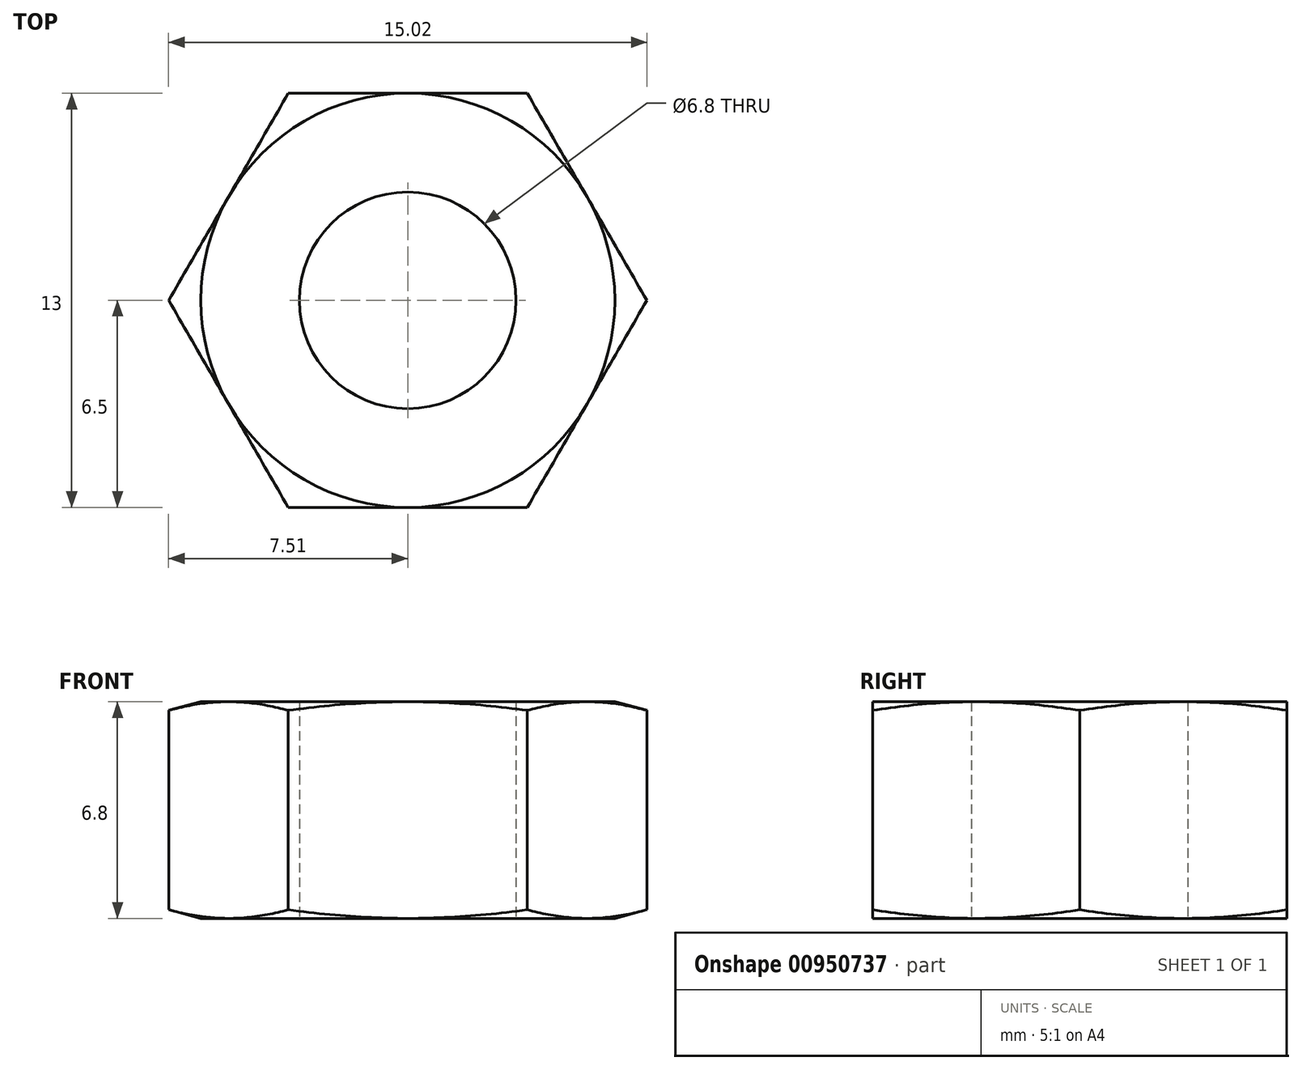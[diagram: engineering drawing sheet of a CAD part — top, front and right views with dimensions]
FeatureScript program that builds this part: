
annotation { "Feature Type Name" : "Feature", "Feature Type Description" : "" }
export const myFeature = defineFeature(function(context is Context, id is Id, definition is map)
    precondition{}
    {
        {
            var Q0;
            Q0=qCreatedBy(makeId("Top.planeOp"),FACE);
            var sketch = newSketch(context, id + "F0", { "sketchPlane" : qUnion([Q0])});
            skCircle(sketch, "E0.cCircle", {"center": v(0, 0) * mm, "radius": 6.5 * mm, "construction": true});
            skLineSegment(sketch, "E0.0", {"start": v(3.75, -6.5) * mm, "end": v(-3.75, -6.5) * mm});
            skLineSegment(sketch, "E0.1", {"start": v(-3.75, -6.5) * mm, "end": v(-7.5, 0) * mm});
            skLineSegment(sketch, "E0.2", {"start": v(-7.5, 0) * mm, "end": v(-3.75, 6.5) * mm});
            skLineSegment(sketch, "E0.3", {"start": v(-3.75, 6.5) * mm, "end": v(3.75, 6.5) * mm});
            skLineSegment(sketch, "E0.4", {"start": v(3.75, 6.5) * mm, "end": v(7.5, 0) * mm});
            skLineSegment(sketch, "E0.5", {"start": v(7.5, 0) * mm, "end": v(3.75, -6.5) * mm});
            skPoint(sketch, "E0.0.midPoint", {"position": v(0, -6.5) * mm});
            skCircle(sketch, "E1", {"center": v(0, 0) * mm, "radius": 3.4 * mm});
            skSolve(sketch);
        }
        {
            var Q0;
            Q0=qSketchRegion(id+"F0",true);
            extrude(context, id + "F1", {"entities" : qUnion([Q0]), "depth" : 6.8 * mm, "offsetDistance" : 25 * mm});
        }
        {
            var Q0;
            Q0=qCreatedBy(makeId("Front.planeOp"),FACE);
            var sketch = newSketch(context, id + "F2", { "sketchPlane" : qUnion([Q0])});
            skLineSegment(sketch, "E2", {"start": v(-6.5, 0) * mm, "end": v(-7.5, 0.27) * mm});
            skLineSegment(sketch, "E3", {"start": v(-7.5, 0.27) * mm, "end": v(-7.5, 0) * mm});
            skLineSegment(sketch, "E4", {"start": v(-7.5, 0) * mm, "end": v(-6.5, 0) * mm});
            skLineSegment(sketch, "E5", {"start": v(-7.5, 6.53) * mm, "end": v(-6.5, 6.8) * mm});
            skLineSegment(sketch, "E6", {"start": v(-6.5, 6.8) * mm, "end": v(-7.5, 6.8) * mm});
            skLineSegment(sketch, "E7", {"start": v(-7.5, 6.8) * mm, "end": v(-7.5, 6.53) * mm});
            skLineSegment(sketch, "E8", {"start": v(0, -2.48) * mm, "end": v(0, 13.77) * mm, "construction": true});
            skSolve(sketch);
        }
        {
            var Q0;
            Q0=qSketchRegion(id+"F2",true);
            var Q1;
            Q1=sQuery(id+"F2.wireOp",EDGE,"E8");
            revolve(context, id + "F3", {"operationType" : NewBodyOperationType.REMOVE, "surfaceOperationType" : NewSurfaceOperationType.NEW, "entities" : qUnion([Q0]), "axis" : qUnion([Q1]), "revolveType" : RevolveType.FULL, "oppositeDirection" : true});
        }
    });
